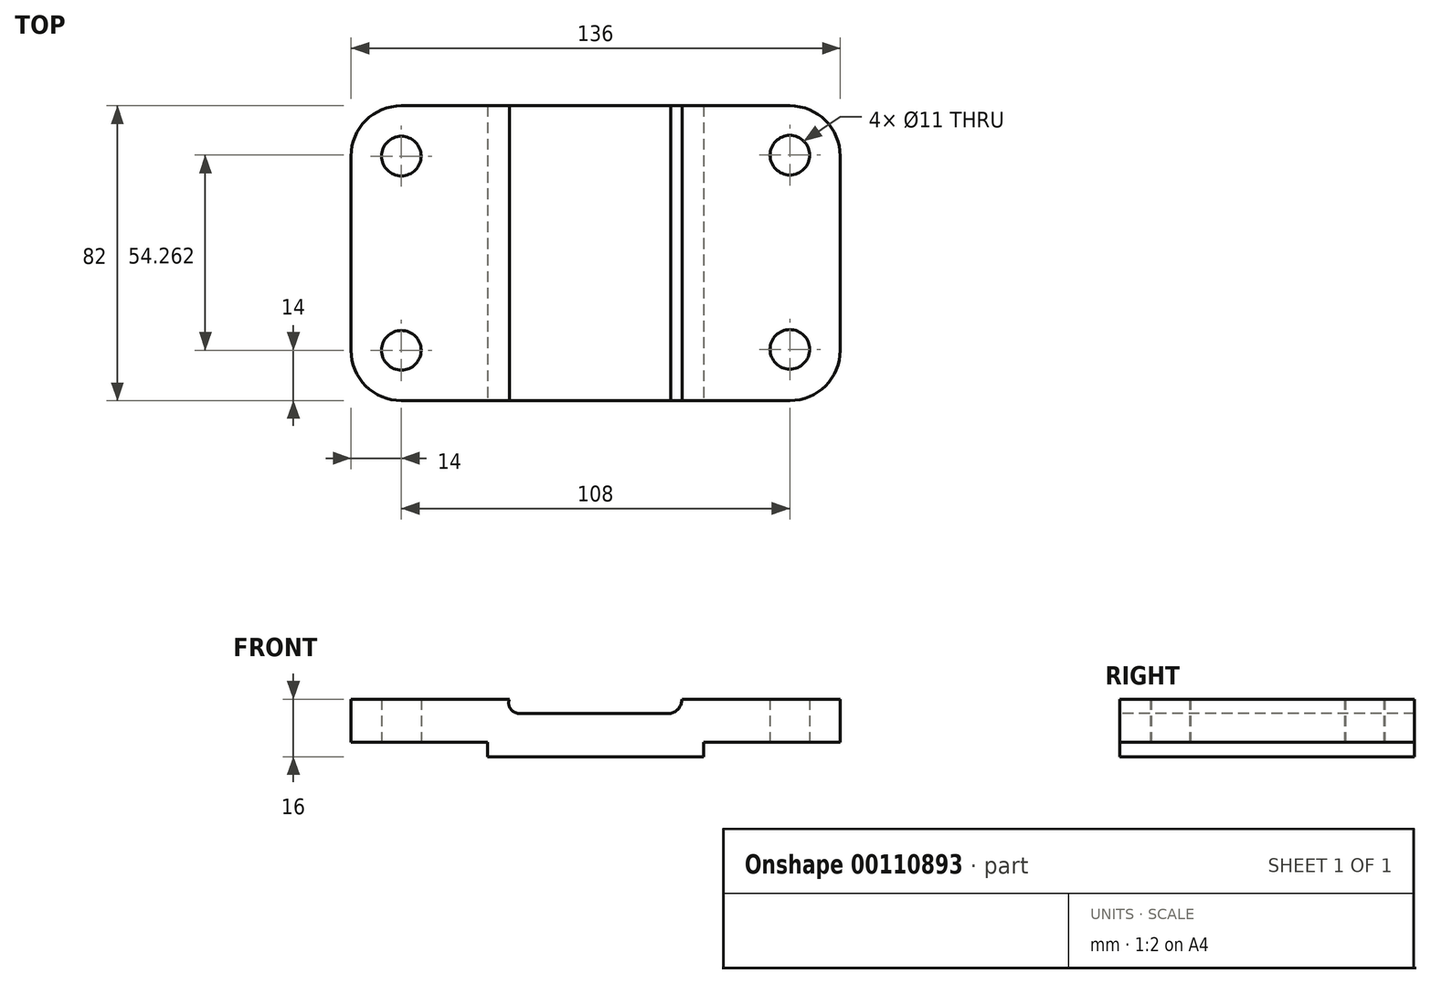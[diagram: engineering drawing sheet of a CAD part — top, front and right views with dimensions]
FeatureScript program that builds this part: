
annotation { "Feature Type Name" : "Feature", "Feature Type Description" : "" }
export const myFeature = defineFeature(function(context is Context, id is Id, definition is map)
    precondition{}
    {
        {
            var Q0;
            Q0=qCreatedBy(makeId("Top.planeOp"),FACE);
            var sketch = newSketch(context, id + "F0", { "sketchPlane" : qUnion([Q0])});
            skLineSegment(sketch, "E0", {"start": v(0, 0) * mm, "end": v(0, 82) * mm});
            skLineSegment(sketch, "E1", {"start": v(0, 82) * mm, "end": v(136, 82) * mm});
            skLineSegment(sketch, "E2", {"start": v(136, 82) * mm, "end": v(136, 0) * mm});
            skLineSegment(sketch, "E3", {"start": v(136, 0) * mm, "end": v(0, 0) * mm});
            skArc(sketch, "E4", {"start": v(14, 82) * mm, "mid": v(4.1, 77.9) * mm, "end": v(0, 68) * mm});
            skArc(sketch, "E5", {"start": v(136, 68) * mm, "mid": v(131.9, 77.9) * mm, "end": v(122, 82) * mm});
            skArc(sketch, "E6", {"start": v(0, 14) * mm, "mid": v(4.1, 4.1) * mm, "end": v(14, 0) * mm});
            skArc(sketch, "E7", {"start": v(122, 0) * mm, "mid": v(131.9, 4.1) * mm, "end": v(136, 14) * mm});
            skLineSegment(sketch, "E8", {"start": v(136, 68) * mm, "end": v(136, 14) * mm});
            skCircle(sketch, "E9", {"center": v(14, 68) * mm, "radius": 5.5 * mm});
            skCircle(sketch, "E10.0.1.0", {"center": v(14, 14) * mm, "radius": 5.5 * mm});
            skCircle(sketch, "E10.1.0.0", {"center": v(122, 68.26) * mm, "radius": 5.5 * mm});
            skCircle(sketch, "E10.1.1.0", {"center": v(122, 14.26) * mm, "radius": 5.5 * mm});
            skLineSegment(sketch, "E10.direction1", {"start": v(14, 68) * mm, "end": v(122, 68.26) * mm, "construction": true});
            skLineSegment(sketch, "E10.direction2", {"start": v(14, 68) * mm, "end": v(14, 14) * mm, "construction": true});
            skLineSegment(sketch, "E11", {"start": v(44, 82) * mm, "end": v(44, 0) * mm});
            skLineSegment(sketch, "E12", {"start": v(92, 82) * mm, "end": v(92, 0) * mm});
            skSolve(sketch);
        }
        {
            var Q0;
            {var subQ0=sQuery(id+"F0.wireOp",EDGE,"E4");Q0=makeQuery(id+"F0.imprint","IMPRINT",FACE,{"disambiguationData":[TD([[makeQuery(id+"F0.imprint","IMPRINT",EDGE,{"derivedFrom":subQ0}),1.0]])]});}
            var Q1;
            {var subQ0=sQuery(id+"F0.wireOp",EDGE,"E11");Q1=makeQuery(id+"F0.imprint","IMPRINT",FACE,{"disambiguationData":[TD([[makeQuery(id+"F0.imprint","IMPRINT",EDGE,{"derivedFrom":subQ0}),1.0]])]});}
            var Q2;
            {var subQ2=sQuery(id+"F0.wireOp",EDGE,"E5");Q2=makeQuery(id+"F0.imprint","IMPRINT",FACE,{"disambiguationData":[TD([[makeQuery(id+"F0.imprint","IMPRINT",EDGE,{"derivedFrom":subQ2}),1.0]])]});}
            extrude(context, id + "F1", {"entities" : qUnion([Q0, Q1, Q2]), "depth" : 16 * mm});
        }
        {
            var Q0;
            Q0=qCreatedBy(makeId("Front.planeOp"),FACE);
            var sketch = newSketch(context, id + "F2", { "sketchPlane" : qUnion([Q0])});
            skLineSegment(sketch, "E13", {"start": v(0, 4) * mm, "end": v(0, 16) * mm});
            skLineSegment(sketch, "E14", {"start": v(0, 4) * mm, "end": v(38, 4) * mm});
            skLineSegment(sketch, "E15", {"start": v(38, 4) * mm, "end": v(38, 0) * mm});
            skLineSegment(sketch, "E16", {"start": v(38, 0) * mm, "end": v(98, 0) * mm});
            skLineSegment(sketch, "E17", {"start": v(98, 0) * mm, "end": v(98, 4) * mm});
            skLineSegment(sketch, "E18", {"start": v(98, 4) * mm, "end": v(136, 4) * mm});
            skLineSegment(sketch, "E19", {"start": v(136, 4) * mm, "end": v(136, 16) * mm});
            skLineSegment(sketch, "E20", {"start": v(136, 16) * mm, "end": v(92, 16) * mm});
            skLineSegment(sketch, "E21", {"start": v(0, 16) * mm, "end": v(44, 16) * mm});
            skLineSegment(sketch, "E22", {"start": v(46.83, 12) * mm, "end": v(88.83, 12) * mm});
            skLineSegment(sketch, "E23", {"start": v(98, 0) * mm, "end": v(38, 0) * mm});
            skLineSegment(sketch, "E24", {"start": v(38, 0) * mm, "end": v(0, 0) * mm, "construction": true});
            skLineSegment(sketch, "E25", {"start": v(98, 0) * mm, "end": v(136, 0) * mm, "construction": true});
            skLineSegment(sketch, "E26", {"start": v(136, 0) * mm, "end": v(136, 4) * mm, "construction": true});
            skArc(sketch, "E27", {"start": v(44, 16) * mm, "mid": v(44.38, 13.27) * mm, "end": v(46.83, 12) * mm});
            skArc(sketch, "E28", {"start": v(88.83, 12) * mm, "mid": v(91.11, 13.45) * mm, "end": v(92, 16) * mm});
            skSolve(sketch);
        }
        {
            var Q0;
            Q0=makeQuery(id+"F2.imprint","IMPRINT",FACE,{"disambiguationData":[TD([[makeQuery(id+"F2.imprint","IMPRINT",EDGE,{"derivedFrom":sQuery(id+"F2.wireOp",EDGE,"E13")}),-1.0]])]});
            extrude(context, id + "F3", {"entities" : qUnion([Q0]), "operationType" : NewBodyOperationType.INTERSECT, "endBound" : BoundingType.THROUGH_ALL, "oppositeDirection" : true, "depth" : 25 * mm});
        }
    });
